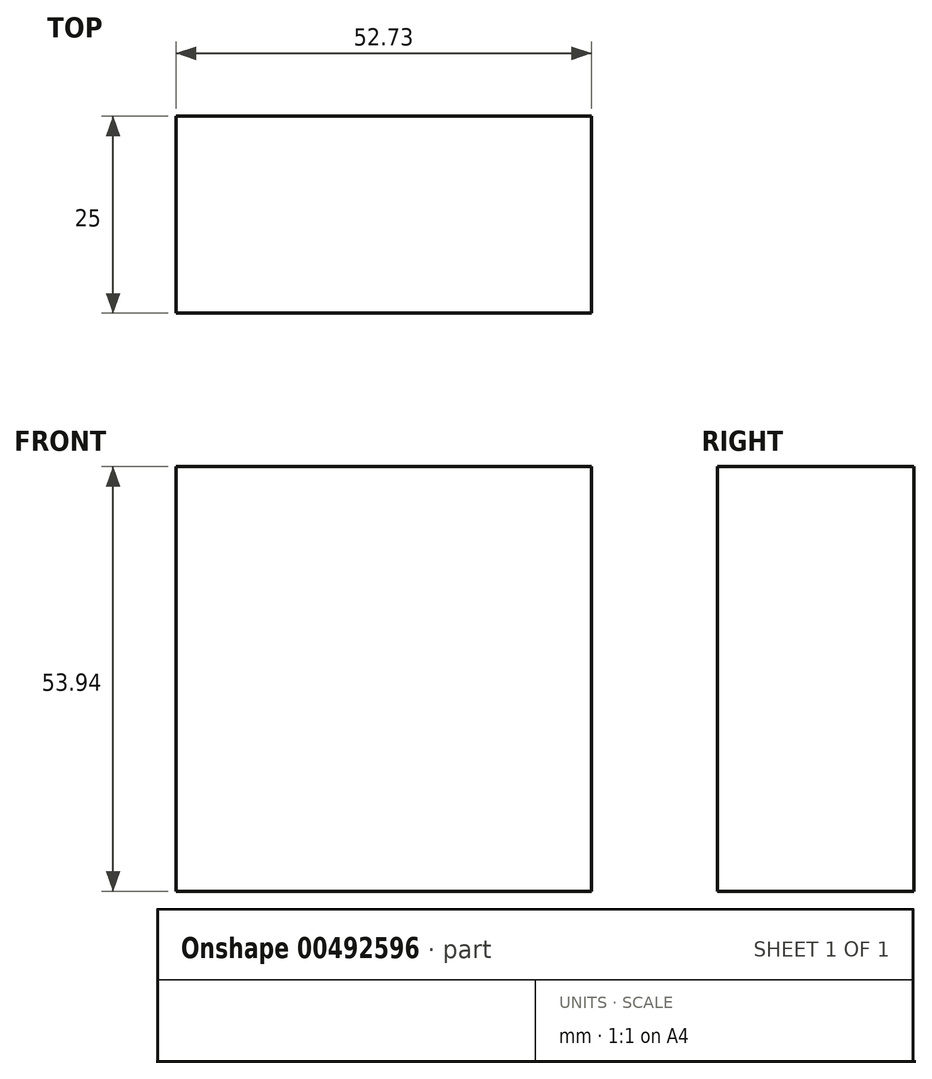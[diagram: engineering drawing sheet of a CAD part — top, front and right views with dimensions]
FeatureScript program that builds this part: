
annotation { "Feature Type Name" : "Feature", "Feature Type Description" : "" }
export const myFeature = defineFeature(function(context is Context, id is Id, definition is map)
    precondition{}
    {
        {
            var Q0;
            Q0=qCreatedBy(makeId("Front.planeOp"),FACE);
            var sketch = newSketch(context, id + "F0", { "sketchPlane" : qUnion([Q0])});
            skLineSegment(sketch, "E0.bottom", {"start": v(-88.45, 12.85) * mm, "end": v(-35.72, 12.85) * mm});
            skLineSegment(sketch, "E0.top", {"start": v(-88.45, 66.8) * mm, "end": v(-35.72, 66.8) * mm});
            skLineSegment(sketch, "E0.left", {"start": v(-88.45, 12.85) * mm, "end": v(-88.45, 66.8) * mm});
            skLineSegment(sketch, "E0.right", {"start": v(-35.72, 12.85) * mm, "end": v(-35.72, 66.8) * mm});
            skPoint(sketch, "E0.middle", {"position": v(-62.08, 39.82) * mm});
            skSolve(sketch);
        }
        {
            var Q0;
            Q0=makeQuery(id+"F0.imprint","IMPRINT",FACE,{"disambiguationData":[TD([[makeQuery(id+"F0.imprint","IMPRINT",EDGE,{"derivedFrom":sQuery(id+"F0.wireOp",EDGE,"E0.bottom")}),1.0]])]});
            extrude(context, id + "F1", {"entities" : qUnion([Q0]), "depth" : 25 * mm});
        }
    });
